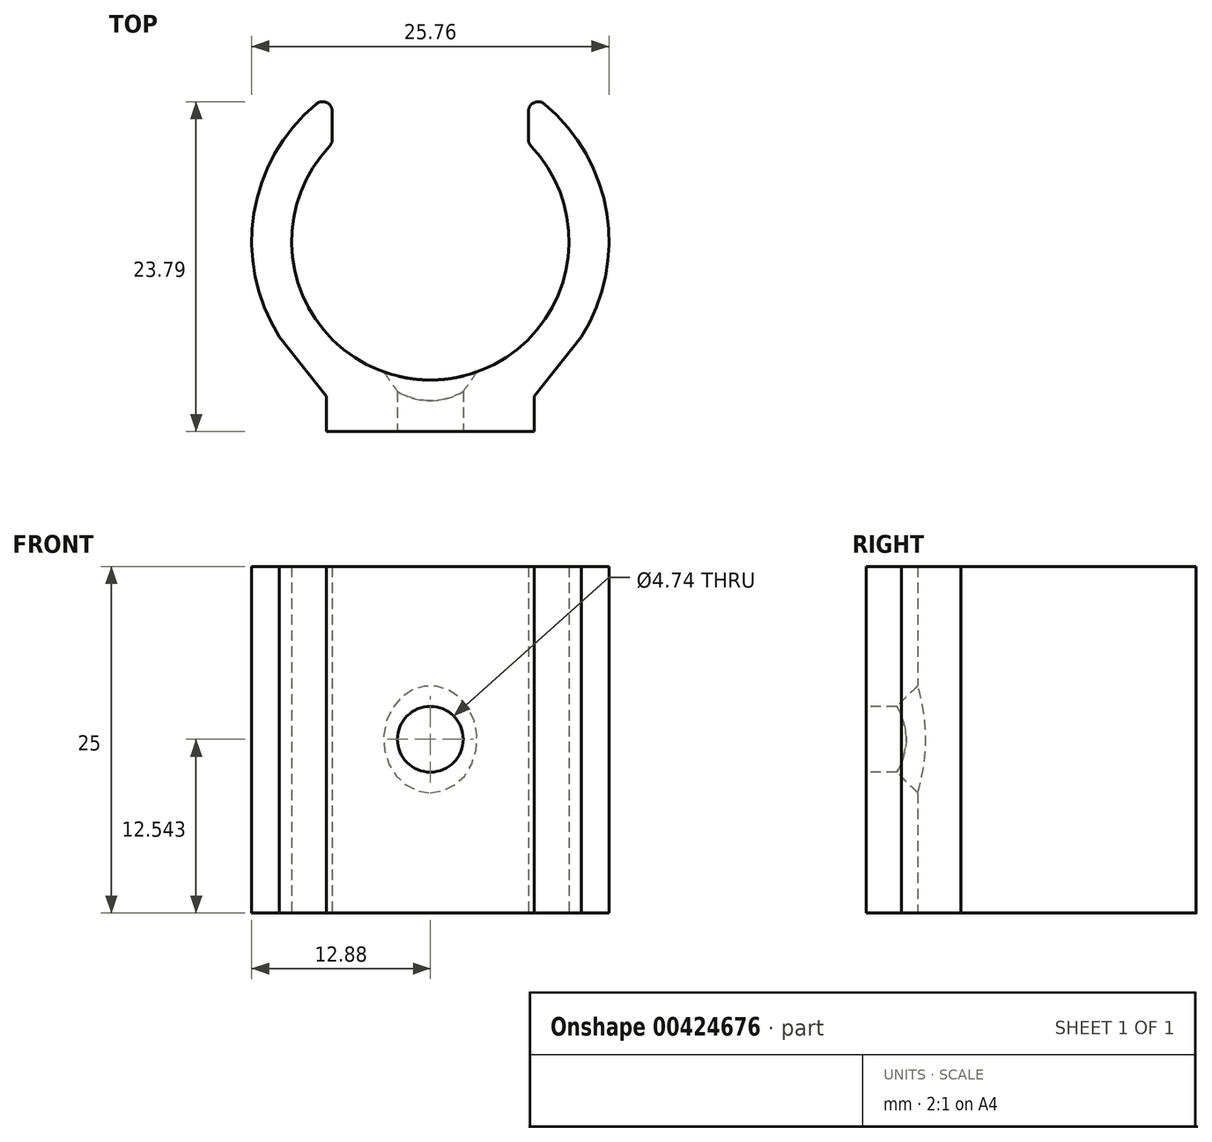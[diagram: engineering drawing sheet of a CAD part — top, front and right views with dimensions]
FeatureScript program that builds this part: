
annotation { "Feature Type Name" : "Feature", "Feature Type Description" : "" }
export const myFeature = defineFeature(function(context is Context, id is Id, definition is map)
    precondition{}
    {
        {
            var Q0;
            Q0=qCreatedBy(makeId("Top.planeOp"),FACE);
            var sketch = newSketch(context, id + "F0", { "sketchPlane" : qUnion([Q0])});
            skArc(sketch, "E0", {"start": v(-7.26, 6.87) * mm, "mid": v(0, -10) * mm, "end": v(7.26, 6.87) * mm});
            skLineSegment(sketch, "E1.top", {"start": v(-7.5, -13.71) * mm, "end": v(7.5, -13.71) * mm});
            skLineSegment(sketch, "E1.left", {"start": v(-7.5, -11.16) * mm, "end": v(-7.5, -13.71) * mm});
            skLineSegment(sketch, "E1.right", {"start": v(7.5, -11.16) * mm, "end": v(7.5, -13.71) * mm});
            skPoint(sketch, "E1.middle", {"position": v(0, -10.21) * mm});
            skArc(sketch, "E2", {"start": v(10.88, -6.9) * mm, "mid": v(12.72, 2.01) * mm, "end": v(8.22, 9.92) * mm});
            skLineSegment(sketch, "E3.left", {"start": v(-7.07, 9.38) * mm, "end": v(-7.07, 7.35) * mm});
            skPoint(sketch, "E3.middle", {"position": v(0, 8.45) * mm});
            skArc(sketch, "E4.trimOffspring", {"start": v(-8.22, 9.92) * mm, "mid": v(-12.72, 2.01) * mm, "end": v(-10.88, -6.9) * mm});
            skPoint(sketch, "E5.orphan", {"position": v(-7.07, 2.56) * mm});
            skPoint(sketch, "E3.right.start.orphan", {"position": v(7.07, 14.34) * mm});
            skPoint(sketch, "E6.trimOffspring.end.orphan", {"position": v(7.07, 2.56) * mm});
            skPoint(sketch, "E7.orphan", {"position": v(-7.07, 14.34) * mm});
            skPoint(sketch, "E8.visualSharp", {"position": v(-7.07, 10.76) * mm});
            skArc(sketch, "E8.filletArc", {"start": v(-7.07, 9.38) * mm, "mid": v(-7.48, 10.01) * mm, "end": v(-8.22, 9.92) * mm});
            skLineSegment(sketch, "E9", {"start": v(7.07, 9.38) * mm, "end": v(7.07, 7.35) * mm});
            skPoint(sketch, "E10.visualSharp", {"position": v(7.07, 10.76) * mm});
            skArc(sketch, "E10.filletArc", {"start": v(8.22, 9.92) * mm, "mid": v(7.48, 10.01) * mm, "end": v(7.07, 9.38) * mm});
            skPoint(sketch, "E11.visualSharp", {"position": v(-7.07, 7.07) * mm});
            skArc(sketch, "E11.filletArc", {"start": v(-7.26, 6.87) * mm, "mid": v(-7.12, 7.1) * mm, "end": v(-7.07, 7.35) * mm});
            skPoint(sketch, "E12.visualSharp", {"position": v(7.07, 7.07) * mm});
            skArc(sketch, "E12.filletArc", {"start": v(7.07, 7.35) * mm, "mid": v(7.12, 7.1) * mm, "end": v(7.26, 6.87) * mm});
            skPoint(sketch, "E13.visualSharp", {"position": v(-7.5, -6.71) * mm});
            skPoint(sketch, "E14.visualSharp", {"position": v(7.5, -6.71) * mm});
            skLineSegment(sketch, "E15", {"start": v(10.88, -6.9) * mm, "end": v(7.5, -11.16) * mm});
            skLineSegment(sketch, "E16", {"start": v(-7.5, -11.16) * mm, "end": v(-10.88, -6.9) * mm});
            skSolve(sketch);
        }
        {
            var Q0;
            Q0=makeQuery(id+"F0.imprint","IMPRINT",FACE,{"disambiguationData":[TD([[makeQuery(id+"F0.imprint","IMPRINT",EDGE,{"derivedFrom":sQuery(id+"F0.wireOp",EDGE,"E0")}),-1.0]])]});
            extrude(context, id + "F1", {"entities" : qUnion([Q0]), "depth" : 25 * mm});
        }
        {
            var Q0;
            Q0=makeQuery(id+"F1.opExtrude","SWEPT_FACE",FACE,{"disambiguationData":[OSD([sQuery(id+"F0.wireOp",EDGE,"E1.top")])]});
            var sketch = newSketch(context, id + "F2", { "sketchPlane" : qUnion([Q0])});
            skCircle(sketch, "E17", {"center": v(0, 12.54) * mm, "radius": 2.37 * mm});
            skPoint(sketch, "E17.centerSnap0", {"position": v(0, 25) * mm});
            skSolve(sketch);
        }
        {
            var Q0;
            Q0=makeQuery(id+"F2.imprint","IMPRINT",FACE,{"disambiguationData":[TD([[makeQuery(id+"F2.imprint","IMPRINT",EDGE,{"derivedFrom":sQuery(id+"F2.wireOp",EDGE,"E17")}),1.0]])]});
            extrude(context, id + "F3", {"entities" : qUnion([Q0]), "operationType" : NewBodyOperationType.REMOVE, "oppositeDirection" : true, "depth" : 25 * mm});
        }
        {
            var Q0;
            Q0=makeQuery(id+"F3.boolean.opBoolean","INTERSECT",EDGE,{"derivedFrom":[makeQuery(id+"F1.opExtrude","SWEPT_FACE",FACE,{"disambiguationData":[OSD([sQuery(id+"F0.wireOp",EDGE,"E0")])]}),makeQuery(id+"F3.opExtrude","SWEPT_FACE",FACE,{"disambiguationData":[OSD([sQuery(id+"F2.wireOp",EDGE,"E17")])]})]});
            chamfer(context, id + "F4", {"entities" : qUnion([Q0]), "width" : 1.5 * mm, "tangentPropagation" : true});
        }
    });
